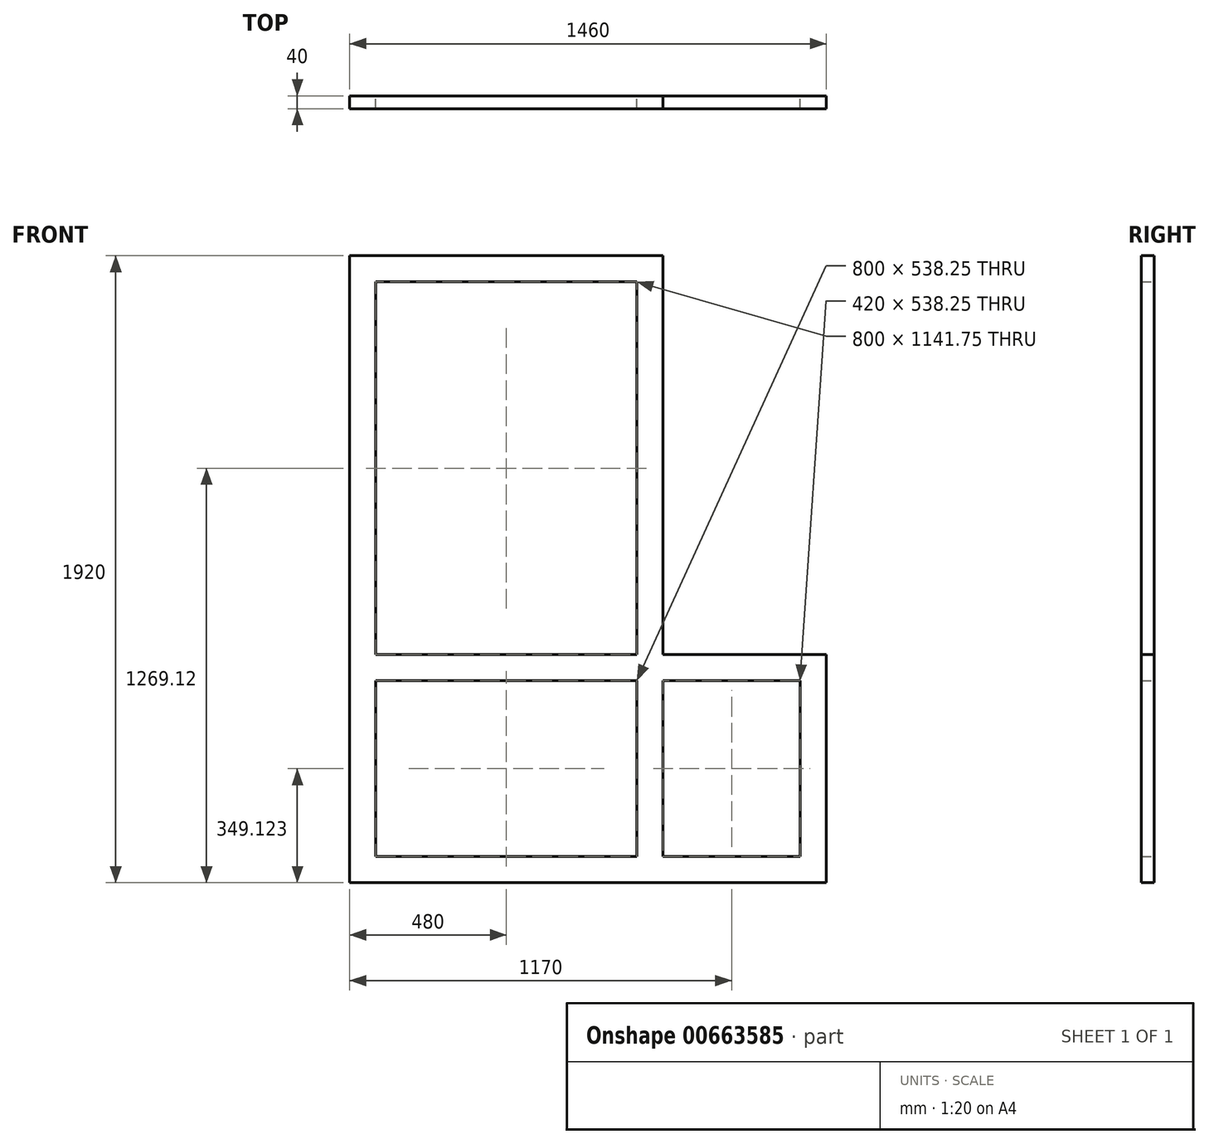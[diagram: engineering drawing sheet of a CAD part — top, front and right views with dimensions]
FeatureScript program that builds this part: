
annotation { "Feature Type Name" : "Feature", "Feature Type Description" : "" }
export const myFeature = defineFeature(function(context is Context, id is Id, definition is map)
    precondition{}
    {
        {
            var Q0;
            Q0=qCreatedBy(makeId("Front.planeOp"),FACE);
            var sketch = newSketch(context, id + "F0", { "sketchPlane" : qUnion([Q0])});
            skLineSegment(sketch, "E0", {"start": v(-80, -80) * mm, "end": v(-80, 1840) * mm});
            skLineSegment(sketch, "E1", {"start": v(-80, 1840) * mm, "end": v(0, 1840) * mm});
            skLineSegment(sketch, "E2", {"start": v(0, 1840) * mm, "end": v(0, -80) * mm});
            skLineSegment(sketch, "E3", {"start": v(0, -80) * mm, "end": v(-80, -80) * mm});
            skLineSegment(sketch, "E4", {"start": v(0, 1840) * mm, "end": v(800, 1840) * mm});
            skLineSegment(sketch, "E5", {"start": v(800, 1840) * mm, "end": v(800, 1760) * mm});
            skLineSegment(sketch, "E6", {"start": v(800, 1760) * mm, "end": v(0, 1760) * mm});
            skLineSegment(sketch, "E7", {"start": v(0, -80) * mm, "end": v(800, -80) * mm});
            skLineSegment(sketch, "E8", {"start": v(800, -80) * mm, "end": v(800, 0) * mm});
            skLineSegment(sketch, "E9", {"start": v(800, 0) * mm, "end": v(0, 0) * mm});
            skLineSegment(sketch, "E10", {"start": v(800, 1840) * mm, "end": v(880, 1840) * mm});
            skLineSegment(sketch, "E11", {"start": v(880, 1840) * mm, "end": v(880, -80) * mm});
            skLineSegment(sketch, "E12", {"start": v(880, -80) * mm, "end": v(800, -80) * mm});
            skLineSegment(sketch, "E13", {"start": v(800, -80) * mm, "end": v(800, 1840) * mm});
            skLineSegment(sketch, "E14", {"start": v(880, -80) * mm, "end": v(1380, -80) * mm});
            skLineSegment(sketch, "E15", {"start": v(1380, -80) * mm, "end": v(1380, 0) * mm});
            skLineSegment(sketch, "E16", {"start": v(1380, 0) * mm, "end": v(880, 0) * mm});
            skLineSegment(sketch, "E17", {"start": v(1380, 0) * mm, "end": v(1380, 618.25) * mm});
            skLineSegment(sketch, "E18", {"start": v(1380, 618.25) * mm, "end": v(880, 618.25) * mm});
            skLineSegment(sketch, "E19.0", {"start": v(1380, 538.25) * mm, "end": v(880, 538.25) * mm});
            skLineSegment(sketch, "E20.0", {"start": v(1300, 0) * mm, "end": v(1300, 618.25) * mm});
            skLineSegment(sketch, "E21", {"start": v(800, 618.25) * mm, "end": v(0, 618.25) * mm});
            skLineSegment(sketch, "E22", {"start": v(800, 538.25) * mm, "end": v(0, 538.25) * mm});
            skSolve(sketch);
        }
        {
            var Q0;
            {var subQ0=sQuery(id+"F0.wireOp",EDGE,"E4");Q0=makeQuery(id+"F0.imprint","IMPRINT",FACE,{"disambiguationData":[TD([[makeQuery(id+"F0.imprint","IMPRINT",EDGE,{"derivedFrom":subQ0}),-1.0]])]});}
            var Q1;
            Q1=makeQuery(id+"F0.imprint","IMPRINT",FACE,{"disambiguationData":[TD([[makeQuery(id+"F0.imprint","IMPRINT",EDGE,{"derivedFrom":sQuery(id+"F0.wireOp",EDGE,"E0")}),-1.0]])]});
            var Q2;
            {var subQ0=sQuery(id+"F0.wireOp",EDGE,"E7");Q2=makeQuery(id+"F0.imprint","IMPRINT",FACE,{"disambiguationData":[TD([[makeQuery(id+"F0.imprint","IMPRINT",EDGE,{"derivedFrom":subQ0}),1.0]])]});}
            var Q3;
            {var subQ3=sQuery(id+"F0.wireOp",EDGE,"E10");Q3=makeQuery(id+"F0.imprint","IMPRINT",FACE,{"disambiguationData":[TD([[makeQuery(id+"F0.imprint","IMPRINT",EDGE,{"derivedFrom":subQ3}),-1.0]])]});}
            extrude(context, id + "F1", {"entities" : qUnion([Q0, Q1, Q2, Q3]), "depth" : 40 * mm, "offsetDistance" : 25 * mm});
        }
        {
            var Q0;
            Q0 = qSketchRegion(id + "F0", true);
            var Q1;
            Q1 = qSketchRegion(id + "F5ZKOOO6Eq69JO8_1", true);
            extrude(context, id + "F2", {"entities" : qUnion([Q0, Q1]), "operationType" : NewBodyOperationType.ADD, "depth" : 40 * mm, "offsetDistance" : 25 * mm});
        }
        {
            var Q0;
            {var subQ0=sQuery(id+"F0.wireOp",EDGE,"E21");Q0=makeQuery(id+"F0.imprint","IMPRINT",FACE,{"disambiguationData":[TD([[makeQuery(id+"F0.imprint","IMPRINT",EDGE,{"derivedFrom":subQ0}),1.0]])]});}
            extrude(context, id + "F3", {"entities" : qUnion([Q0]), "operationType" : NewBodyOperationType.ADD, "depth" : 40 * mm, "offsetDistance" : 25 * mm});
        }
    });
